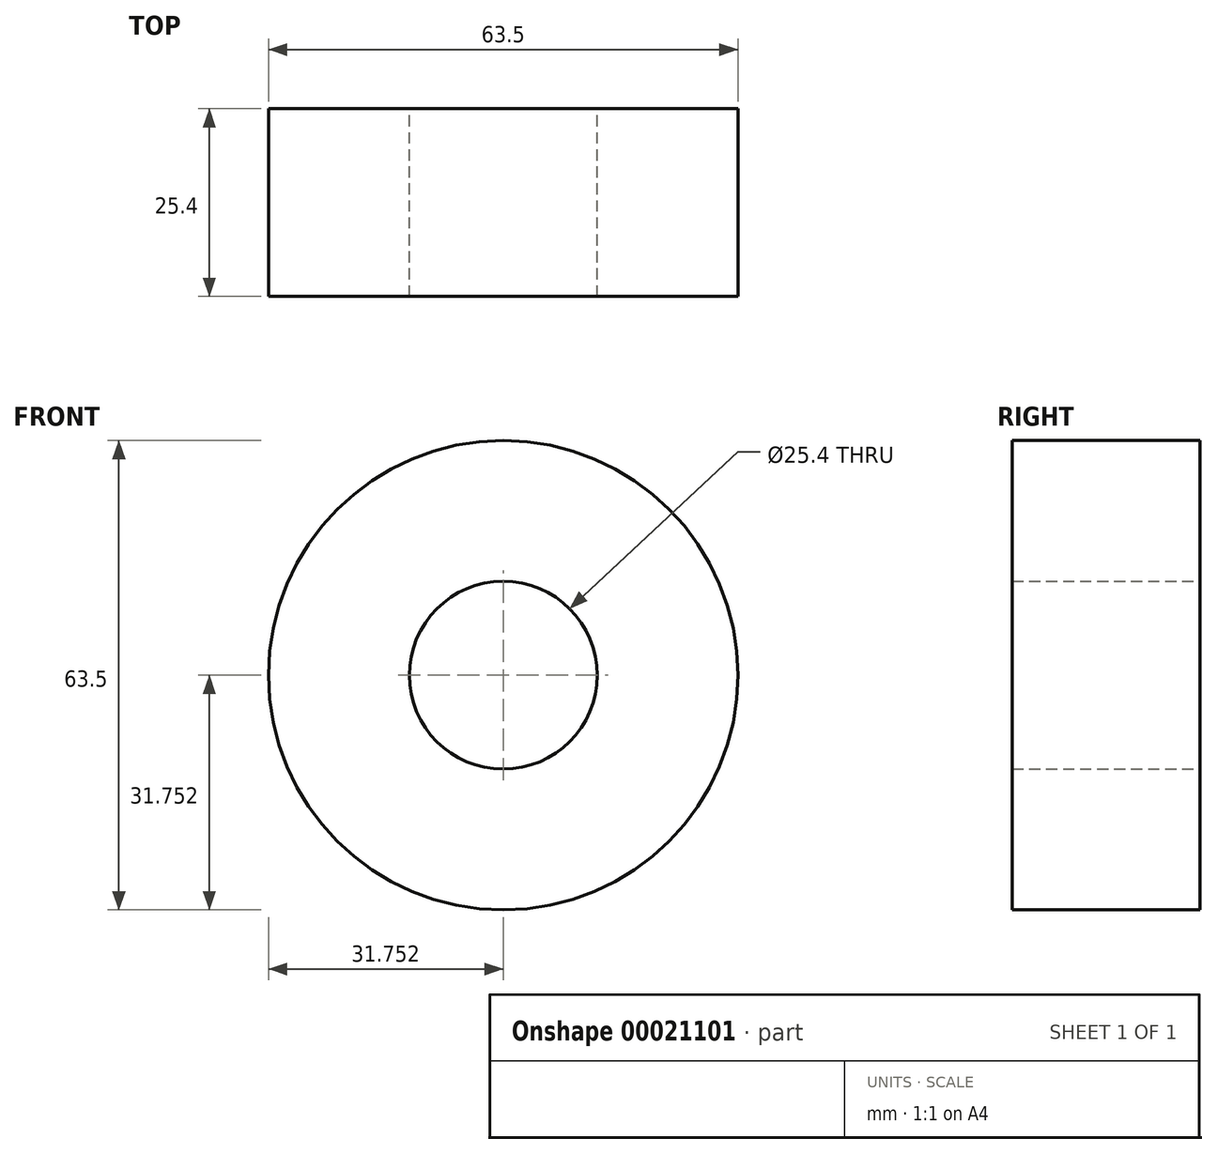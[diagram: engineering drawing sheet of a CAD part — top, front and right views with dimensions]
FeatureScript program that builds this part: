
annotation { "Feature Type Name" : "Feature", "Feature Type Description" : "" }
export const myFeature = defineFeature(function(context is Context, id is Id, definition is map)
    precondition{}
    {
        {
            var Q0;
            Q0=qCreatedBy(makeId("Front.planeOp"),FACE);
            var sketch = newSketch(context, id + "F0", { "sketchPlane" : qUnion([Q0])});
            skLineSegment(sketch, "E0.bottom", {"start": v(-97.15, 53.32) * mm, "end": v(7.63, 53.32) * mm});
            skLineSegment(sketch, "E0.top", {"start": v(-97.15, -10.18) * mm, "end": v(7.63, -10.18) * mm});
            skLineSegment(sketch, "E0.left", {"start": v(-97.15, 53.32) * mm, "end": v(-97.15, -10.18) * mm});
            skLineSegment(sketch, "E0.right", {"start": v(7.63, 53.32) * mm, "end": v(7.63, -10.18) * mm});
            skLineSegment(sketch, "E1.bottom", {"start": v(7.63, -10.18) * mm, "end": v(-97.15, -10.18) * mm});
            skLineSegment(sketch, "E1.top", {"start": v(7.63, 53.32) * mm, "end": v(-97.15, 53.32) * mm});
            skLineSegment(sketch, "E1.left", {"start": v(7.63, -10.18) * mm, "end": v(7.63, 53.32) * mm});
            skLineSegment(sketch, "E1.right", {"start": v(-97.15, -10.18) * mm, "end": v(-97.15, 53.32) * mm});
            skCircle(sketch, "E2", {"center": v(-97.15, 21.57) * mm, "radius": 31.75 * mm});
            skCircle(sketch, "E3", {"center": v(-97.15, 21.57) * mm, "radius": 12.7 * mm});
            skCircle(sketch, "E4", {"center": v(7.63, 53.32) * mm, "radius": 31.75 * mm});
            skSolve(sketch);
        }
        {
            var Q0;
            {var subQ4=sQuery(id+"F0.wireOp",EDGE,"E1.bottom");Q0=makeQuery(id+"F0.imprint","IMPRINT",FACE,{"disambiguationData":[TD([[makeQuery(id+"F0.imprint","IMPRINT",EDGE,{"derivedFrom":subQ4}),-1.0]])]});}
            var Q1;
            {var subQ0=sQuery(id+"F0.wireOp",EDGE,"E3");var subQ1=sQuery(id+"F0.wireOp",EDGE,"E1.right");var subQ3=makeQuery(id+"F0.imprint","INTERSECT",VERTEX,{"disambiguationData":[OD(0.0)],"derivedFrom":[subQ1,subQ0]});Q1=makeQuery(id+"F0.imprint","IMPRINT",FACE,{"disambiguationData":[TD([[makeQuery(id+"F0.imprint","IMPRINT",EDGE,{"disambiguationData":[TD([[subQ3,1.0]])],"derivedFrom":subQ0}),-1.0]])]});}
            var Q2;
            {var subQ0=sQuery(id+"F0.wireOp",EDGE,"E3");var subQ1=sQuery(id+"F0.wireOp",EDGE,"E1.right");var subQ3=makeQuery(id+"F0.imprint","INTERSECT",VERTEX,{"disambiguationData":[OD(0.0)],"derivedFrom":[subQ1,subQ0]});Q2=makeQuery(id+"F0.imprint","IMPRINT",FACE,{"disambiguationData":[TD([[makeQuery(id+"F0.imprint","IMPRINT",EDGE,{"disambiguationData":[TD([[subQ3,-1.0]])],"derivedFrom":subQ0}),-1.0]])]});}
            extrude(context, id + "F1", {"entities" : qUnion([Q0, Q1, Q2]), "depth" : 25.4 * mm});
        }
    });
